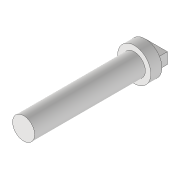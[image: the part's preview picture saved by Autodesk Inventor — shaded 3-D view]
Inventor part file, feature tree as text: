
AUTODESK INVENTOR PART (.ipt)
format: ipt  version: 2020 (Build 240168000, 168)  size: 93,184 bytes
history: native  units: mm
features: extrude x3, sketch x3
ambient origin geometry x8: Origin, YZ Plane, XZ Plane, XY Plane, X Axis, Y Axis, Z Axis, Center Point
bodies: Volumenkörper1 (feature_tree)
feature tree (6):
  extrude  "Extrusion1"  Depth=100.0mm TaperAngle=0.0deg
  extrude  "Extrusion2"  Depth=10.0mm TaperAngle=0.0deg
  extrude  "Extrusion3"  Depth=10.0mm
  sketch  "Skizze1"  dims[d0=20.0mm d1=100.0mm d2=0.0mm]
  sketch  "Skizze2"  dims[d3=30.0mm d4=10.0mm d5=0.0mm]
  sketch  "Skizze3"  dims[d6=20.0mm d7=10.0mm d8=10.0mm d9=0.0mm]
